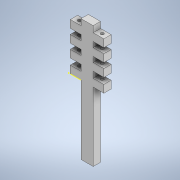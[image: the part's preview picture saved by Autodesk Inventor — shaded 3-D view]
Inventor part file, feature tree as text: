
AUTODESK INVENTOR PART (.ipt)
format: ipt  version: 2020 (Build 240168000, 168)  size: 167,424 bytes
history: native  units: in
note: dims shown in document units (in); Inventor stores cm internally (conversion verified against a paired STEP export)
features: reference x4, sketch x3, other x3, extrude x2, plane x1, projected_geometry x1
ambient origin geometry x8: Origin, YZ Plane, XZ Plane, XY Plane, X Axis, Y Axis, Z Axis, Center Point
bodies: Solid1 (feature_tree)
feature tree (14):
  plane  "Work Plane1"
  extrude  "Extrusion1"  Depth=0.689in
  sketch  "Sketch2"  dims[d2=0.689in d3=0.4921in]
  extrude  "Extrusion2"  Depth=0.4921in
  sketch  "Sketch1"  dims[d0=7.874in d1=0.689in]
  reference  "Reference1"
  reference  "Reference2"
  projected_geometry  "Projected Loop1"
  sketch  "Sketch3"  dims[d4=0.3937in d5=0.0in d7=0.1969in d8=3.3937in d9=0.0in]
  reference  "Reference3"
  reference  "Reference4"
  other  "Assembly3.iam"
  other  "Part9 scaled:1"
  other  "Part9 scaled:2"
